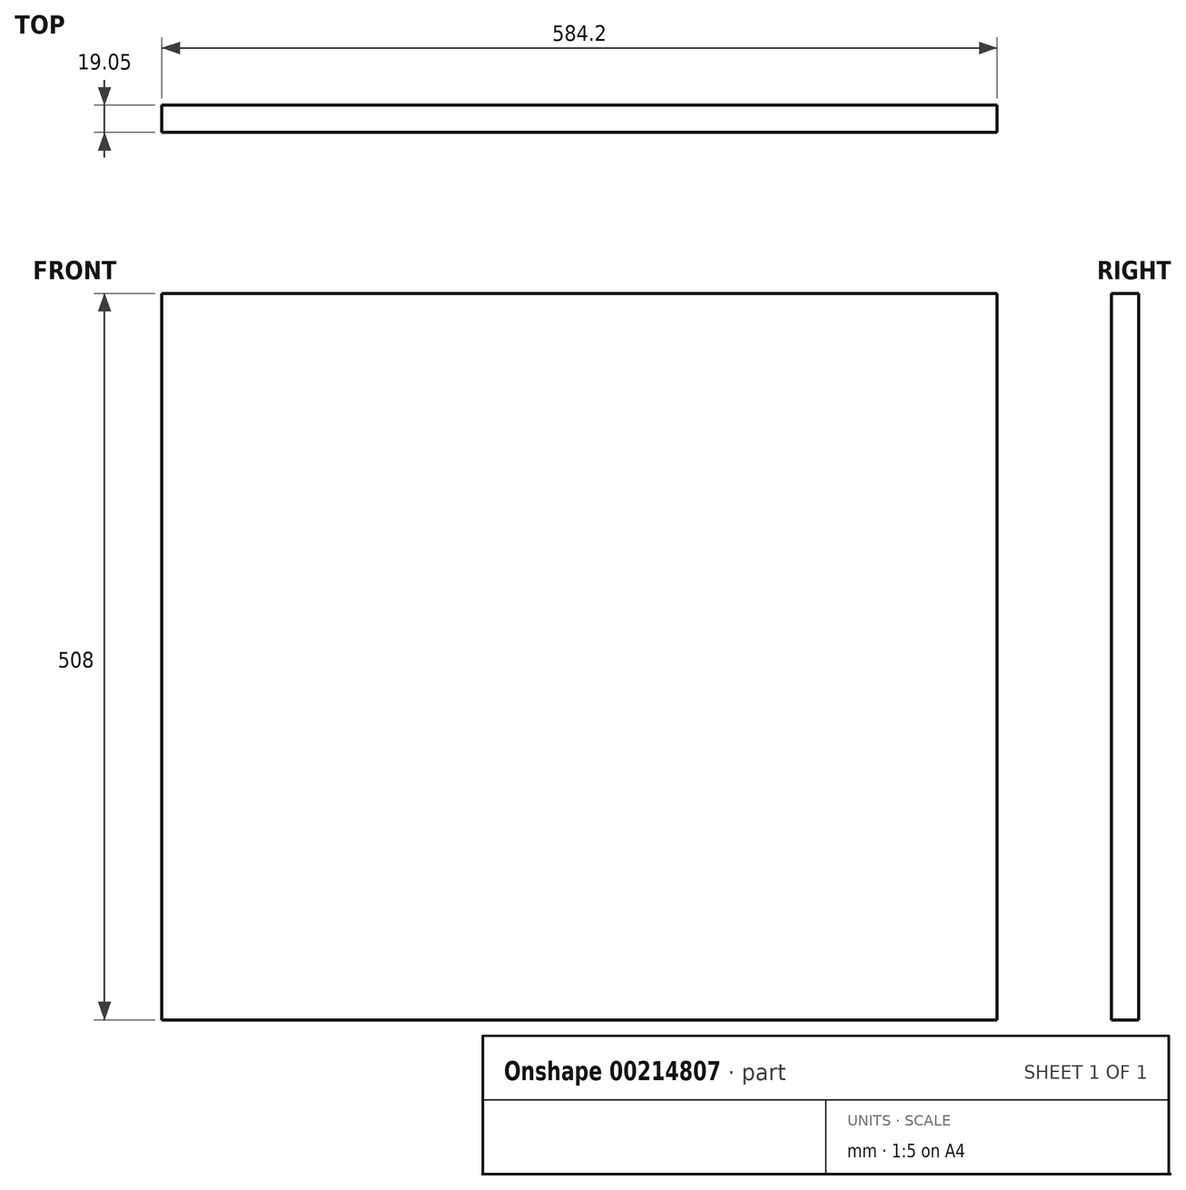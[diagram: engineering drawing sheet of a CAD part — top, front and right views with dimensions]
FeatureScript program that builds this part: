
annotation { "Feature Type Name" : "Feature", "Feature Type Description" : "" }
export const myFeature = defineFeature(function(context is Context, id is Id, definition is map)
    precondition{}
    {
        {
            var Q0;
            Q0=qCreatedBy(makeId("Front.planeOp"),FACE);
            var sketch = newSketch(context, id + "F0", { "sketchPlane" : qUnion([Q0])});
            skLineSegment(sketch, "E0.bottom", {"start": v(0, 0) * mm, "end": v(584.2, 0) * mm});
            skLineSegment(sketch, "E0.top", {"start": v(0, -508) * mm, "end": v(584.2, -508) * mm});
            skLineSegment(sketch, "E0.left", {"start": v(0, 0) * mm, "end": v(0, -508) * mm});
            skLineSegment(sketch, "E0.right", {"start": v(584.2, 0) * mm, "end": v(584.2, -508) * mm});
            skSolve(sketch);
        }
        {
            var Q0;
            Q0=makeQuery(id+"F0.imprint","IMPRINT",FACE,{"disambiguationData":[TD([[makeQuery(id+"F0.imprint","IMPRINT",EDGE,{"derivedFrom":sQuery(id+"F0.wireOp",EDGE,"E0.bottom")}),-1.0]])]});
            extrude(context, id + "F1", {"entities" : qUnion([Q0]), "depth" : 19.05 * mm});
        }
    });
